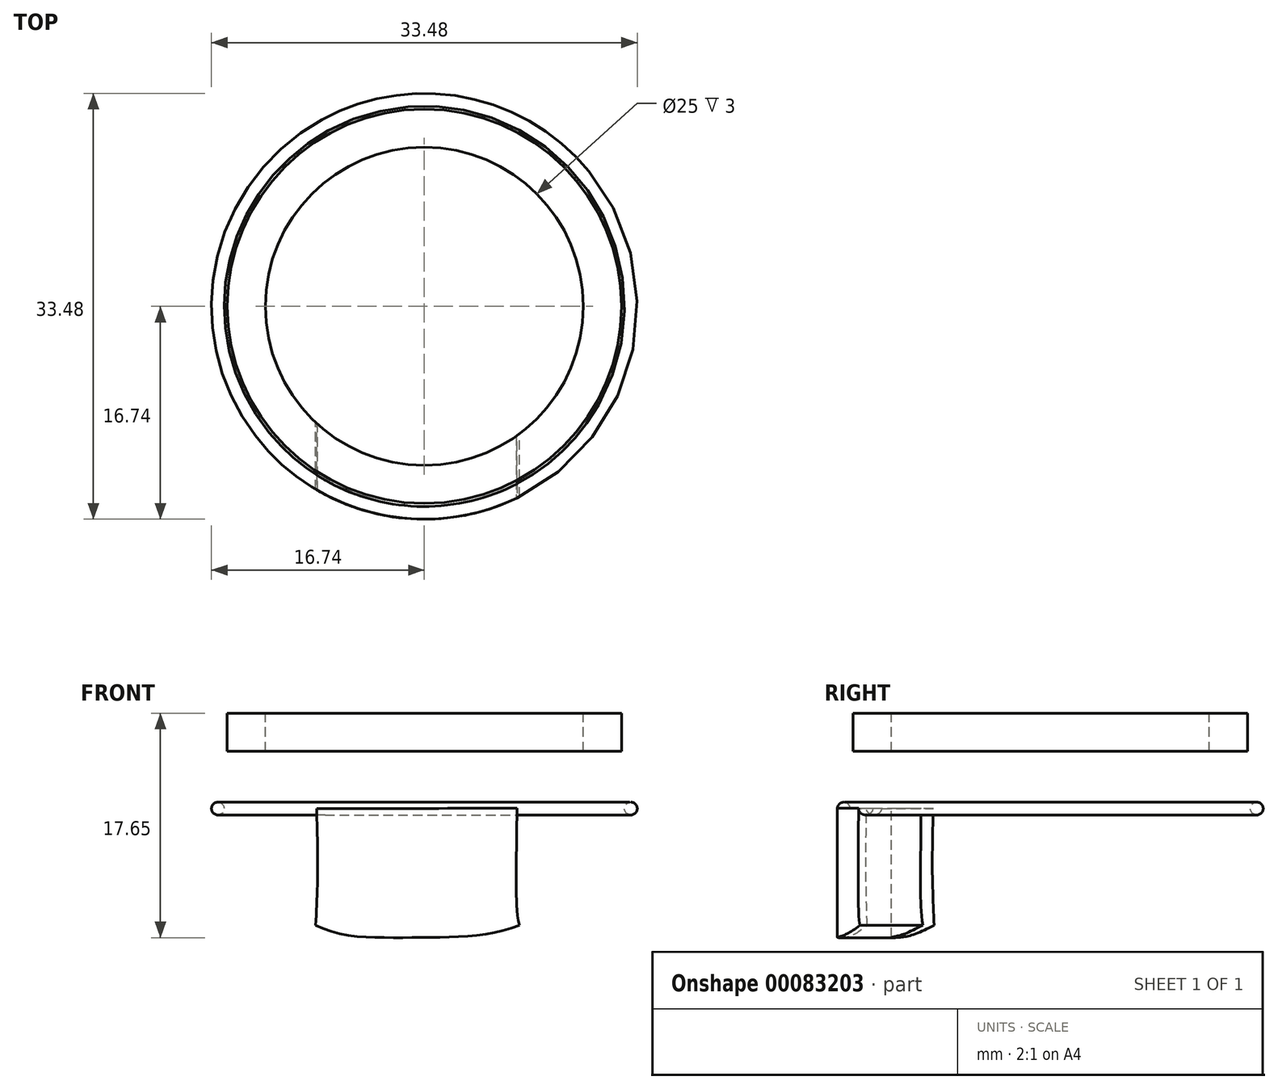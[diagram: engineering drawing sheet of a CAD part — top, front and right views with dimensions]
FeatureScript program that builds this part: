
annotation { "Feature Type Name" : "Feature", "Feature Type Description" : "" }
export const myFeature = defineFeature(function(context is Context, id is Id, definition is map)
    precondition{}
    {
        {
            var Q0;
            Q0=qCreatedBy(makeId("Front.planeOp"),FACE);
            var sketch = newSketch(context, id + "F0", { "sketchPlane" : qUnion([Q0])});
            skLineSegment(sketch, "E0.bottom", {"start": v(17.5, -25) * mm, "end": v(-17.5, -25) * mm});
            skLineSegment(sketch, "E0.top", {"start": v(17.5, 25) * mm, "end": v(-17.5, 25) * mm});
            skLineSegment(sketch, "E0.left", {"start": v(17.5, -25) * mm, "end": v(17.5, 25) * mm});
            skLineSegment(sketch, "E0.right", {"start": v(-17.5, -25) * mm, "end": v(-17.5, 25) * mm});
            skPoint(sketch, "E0.middle", {"position": v(0, 0) * mm});
            skLineSegment(sketch, "E1", {"start": v(-27.91, -5) * mm, "end": v(35.26, -5) * mm});
            skSolve(sketch);
        }
        {
            var Q0;
            {var subQ0=sQuery(id+"F0.wireOp",EDGE,"E0.bottom");Q0=makeQuery(id+"F0.imprint","IMPRINT",FACE,{"disambiguationData":[TD([[makeQuery(id+"F0.imprint","IMPRINT",EDGE,{"derivedFrom":subQ0}),-1.0]])]});}
            var sketch = newSketch(context, id + "F1", { "sketchPlane" : qUnion([Q0])});
            skPoint(sketch, "E2.0", {"position": v(-27.91, -5) * mm});
            skLineSegment(sketch, "E3", {"start": v(0, -2) * mm, "end": v(0, -25) * mm});
            skPoint(sketch, "E4.0", {"position": v(-17.5, -25) * mm});
            skPoint(sketch, "E5.orphan", {"position": v(0, -5) * mm});
            skCircle(sketch, "E6", {"center": v(-16.24, -12.5) * mm, "radius": 0.5 * mm});
            skSolve(sketch);
        }
        {
            var Q0;
            Q0=qSketchRegion(id+"F1",true);
            var Q1;
            Q1=sQuery(id+"F1.wireOp",EDGE,"E3");
            revolve(context, id + "F2", {"entities" : qUnion([Q0]), "axis" : qUnion([Q1]), "revolveType" : RevolveType.FULL});
        }
        {
            var Q0;
            Q0=qCreatedBy(makeId("Front.planeOp"),FACE);
            var sketch = newSketch(context, id + "F3", { "sketchPlane" : qUnion([Q0])});
            skFitSpline(sketch, "E7", {"points": [v(-8.47, -12.52) * mm, v(-8.39, -17.45) * mm, v(-8.54, -21.7) * mm], "startDerivative": vector(0.27, -9.7) * mm, "endDerivative": vector(-0.43, -8.65) * mm});
            skFitSpline(sketch, "E8", {"points": [v(-8.54, -21.7) * mm, v(-6.33, -22.42) * mm, v(-1.56, -22.65) * mm, v(4.86, -22.37) * mm, v(7.47, -21.7) * mm], "startDerivative": vector(10.45, -4.35) * mm, "endDerivative": vector(10.88, 3.73) * mm});
            skFitSpline(sketch, "E9", {"points": [v(7.29, -12.47) * mm, v(7.24, -15.77) * mm, v(7.29, -20.54) * mm, v(7.47, -21.7) * mm], "startDerivative": vector(-0.12, -8.3) * mm, "endDerivative": vector(0.99, -4.3) * mm});
            skLineSegment(sketch, "E10", {"start": v(-8.47, -12.52) * mm, "end": v(7.29, -12.47) * mm});
            skLineSegment(sketch, "E11", {"start": v(-8.47, -12.52) * mm, "end": v(0, -12.5) * mm});
            skSolve(sketch);
        }
        {
            var Q0;
            Q0=makeQuery(id+"F3.imprint","IMPRINT",FACE,{"disambiguationData":[TD([[makeQuery(id+"F3.imprint","IMPRINT",EDGE,{"derivedFrom":sQuery(id+"F3.wireOp",EDGE,"E7")}),1.0]])]});
            var Q1;
            Q1=sQuery(id+"F3.wireOp",EDGE,"E11");
            var Q2;
            Q2=sQuery(id+"F3.wireOp",EDGE,"E10");
            var Q3;
            Q3=sQuery(id+"F3.wireOp",EDGE,"E7");
            var Q4;
            Q4=sQuery(id+"F3.wireOp",EDGE,"E8");
            var Q5;
            Q5=sQuery(id+"F3.wireOp",EDGE,"E9");
            var Q6;
            Q6=makeQuery(id+"F2.opRevolve","SWEPT_FACE",FACE,{"disambiguationData":[OSD([sQuery(id+"F1.wireOp",EDGE,"E6")])]});
            var Q7;
            Q7=makeQuery(id+"F2.opRevolve","SWEPT_BODY",BODY,{"disambiguationData":[OSD([sQuery(id+"F1.wireOp",EDGE,"E6")])]});
            extrude(context, id + "F4", {"entities" : qUnion([Q0]), "operationType" : NewBodyOperationType.ADD, "surfaceEntities" : qUnion([Q1, Q2, Q3, Q4, Q5]), "endBoundEntityFace" : qUnion([Q6]), "endBoundEntityBody" : qUnion([Q7]), "depth" : 20 * mm});
        }
        {
            var Q0;
            Q0=qCreatedBy(makeId("Front.planeOp"),FACE);
            var sketch = newSketch(context, id + "F5", { "sketchPlane" : qUnion([Q0])});
            skLineSegment(sketch, "E12.bottom", {"start": v(-26.74, -12.4) * mm, "end": v(-16.74, -12.4) * mm});
            skLineSegment(sketch, "E12.top", {"start": v(-26.74, -22.84) * mm, "end": v(-16.74, -22.84) * mm});
            skLineSegment(sketch, "E12.left", {"start": v(-26.74, -12.4) * mm, "end": v(-26.74, -22.84) * mm});
            skLineSegment(sketch, "E12.right", {"start": v(-16.74, -12.4) * mm, "end": v(-16.74, -22.84) * mm});
            skLineSegment(sketch, "E13", {"start": v(0, 0) * mm, "end": v(0, -33.42) * mm});
            skSolve(sketch);
        }
        {
            var Q0;
            Q0=makeQuery(id+"F5.imprint","IMPRINT",FACE,{"disambiguationData":[TD([[makeQuery(id+"F5.imprint","IMPRINT",EDGE,{"derivedFrom":sQuery(id+"F5.wireOp",EDGE,"E12.bottom")}),-1.0]])]});
            var Q1;
            Q1=sQuery(id+"F5.wireOp",EDGE,"E13");
            revolve(context, id + "F6", {"operationType" : NewBodyOperationType.REMOVE, "entities" : qUnion([Q0]), "axis" : qUnion([Q1]), "revolveType" : RevolveType.FULL, "oppositeDirection" : true});
        }
        {
            var Q0;
            Q0=qCreatedBy(makeId("Front.planeOp"),FACE);
            var sketch = newSketch(context, id + "F7", { "sketchPlane" : qUnion([Q0])});
            skLineSegment(sketch, "E14", {"start": v(0, -5) * mm, "end": v(-15.5, -5) * mm});
            skLineSegment(sketch, "E15", {"start": v(-15.5, -5) * mm, "end": v(-15.5, -8) * mm});
            skLineSegment(sketch, "E16", {"start": v(-15.5, -8) * mm, "end": v(0, -8) * mm});
            skLineSegment(sketch, "E17", {"start": v(0, -8) * mm, "end": v(0, -5) * mm});
            skSolve(sketch);
        }
        {
            var Q0;
            Q0=makeQuery(id+"F7.imprint","IMPRINT",FACE,{"disambiguationData":[TD([[makeQuery(id+"F7.imprint","IMPRINT",EDGE,{"derivedFrom":sQuery(id+"F7.wireOp",EDGE,"E14")}),1.0]])]});
            var Q1;
            Q1=sQuery(id+"F7.wireOp",EDGE,"E17");
            revolve(context, id + "F8", {"entities" : qUnion([Q0]), "axis" : qUnion([Q1]), "revolveType" : RevolveType.FULL});
        }
        {
            var Q0;
            Q0=makeQuery(id+"F8.opRevolve","SWEPT_FACE",FACE,{"disambiguationData":[OSD([sQuery(id+"F7.wireOp",EDGE,"E14")])]});
            var sketch = newSketch(context, id + "F9", { "sketchPlane" : qUnion([Q0])});
            skCircle(sketch, "E18", {"center": v(0, 0) * mm, "radius": 12.5 * mm});
            skSolve(sketch);
        }
        {
            var Q0;
            Q0=makeQuery(id+"F9.imprint","IMPRINT",FACE,{"disambiguationData":[TD([[makeQuery(id+"F9.imprint","IMPRINT",EDGE,{"derivedFrom":sQuery(id+"F9.wireOp",EDGE,"E18")}),1.0]])]});
            extrude(context, id + "F10", {"entities" : qUnion([Q0]), "operationType" : NewBodyOperationType.REMOVE, "endBound" : BoundingType.THROUGH_ALL, "oppositeDirection" : true, "depth" : 25 * mm});
        }
    });
